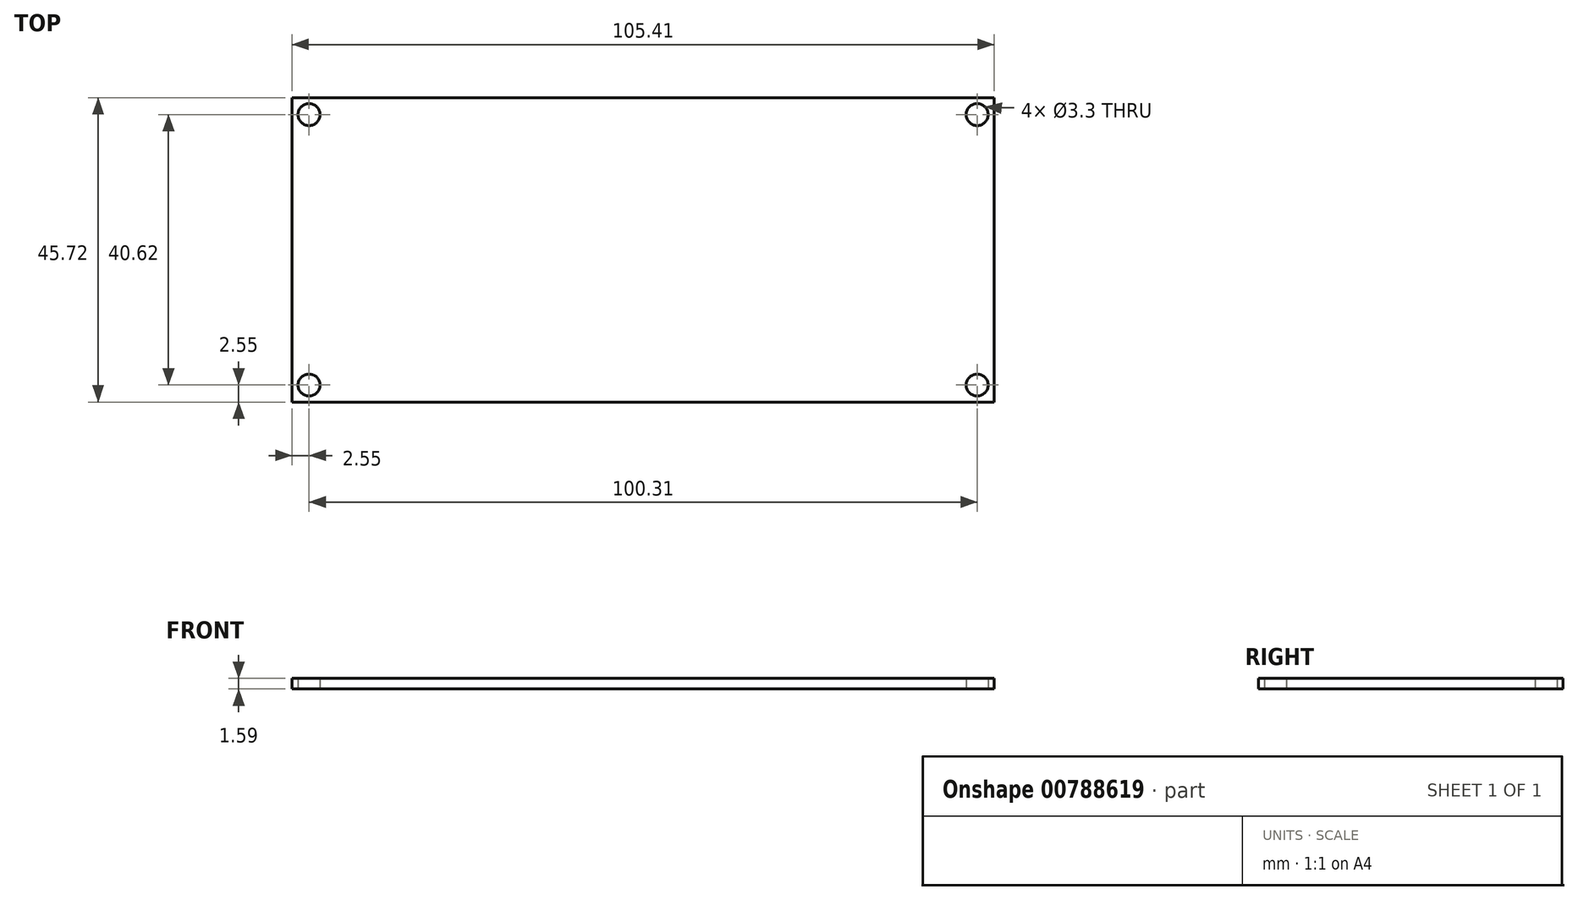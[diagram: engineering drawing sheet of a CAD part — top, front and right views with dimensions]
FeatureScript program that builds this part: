
annotation { "Feature Type Name" : "Feature", "Feature Type Description" : "" }
export const myFeature = defineFeature(function(context is Context, id is Id, definition is map)
    precondition{}
    {
        {
            var Q0;
            Q0=qCreatedBy(makeId("Top.planeOp"),FACE);
            var sketch = newSketch(context, id + "F0", { "sketchPlane" : qUnion([Q0])});
            skLineSegment(sketch, "E0.bottom", {"start": v(0, 0) * mm, "end": v(105.41, 0) * mm});
            skLineSegment(sketch, "E0.top", {"start": v(0, 45.72) * mm, "end": v(105.41, 45.72) * mm});
            skLineSegment(sketch, "E0.left", {"start": v(0, 0) * mm, "end": v(0, 45.72) * mm});
            skLineSegment(sketch, "E0.right", {"start": v(105.41, 0) * mm, "end": v(105.41, 45.72) * mm});
            skCircle(sketch, "E1", {"center": v(2.55, 43.17) * mm, "radius": 1.65 * mm});
            skCircle(sketch, "E2", {"center": v(102.86, 43.17) * mm, "radius": 1.65 * mm});
            skCircle(sketch, "E3", {"center": v(102.86, 2.55) * mm, "radius": 1.65 * mm});
            skCircle(sketch, "E4", {"center": v(2.55, 2.55) * mm, "radius": 1.65 * mm});
            skSolve(sketch);
        }
        {
            var Q0;
            Q0=makeQuery(id+"F0.imprint","IMPRINT",FACE,{"disambiguationData":[TD([[makeQuery(id+"F0.imprint","IMPRINT",EDGE,{"derivedFrom":sQuery(id+"F0.wireOp",EDGE,"E0.bottom")}),1.0]])]});
            extrude(context, id + "F1", {"entities" : qUnion([Q0]), "depth" : 1.59 * mm, "offsetDistance" : 25.4 * mm});
        }
    });
